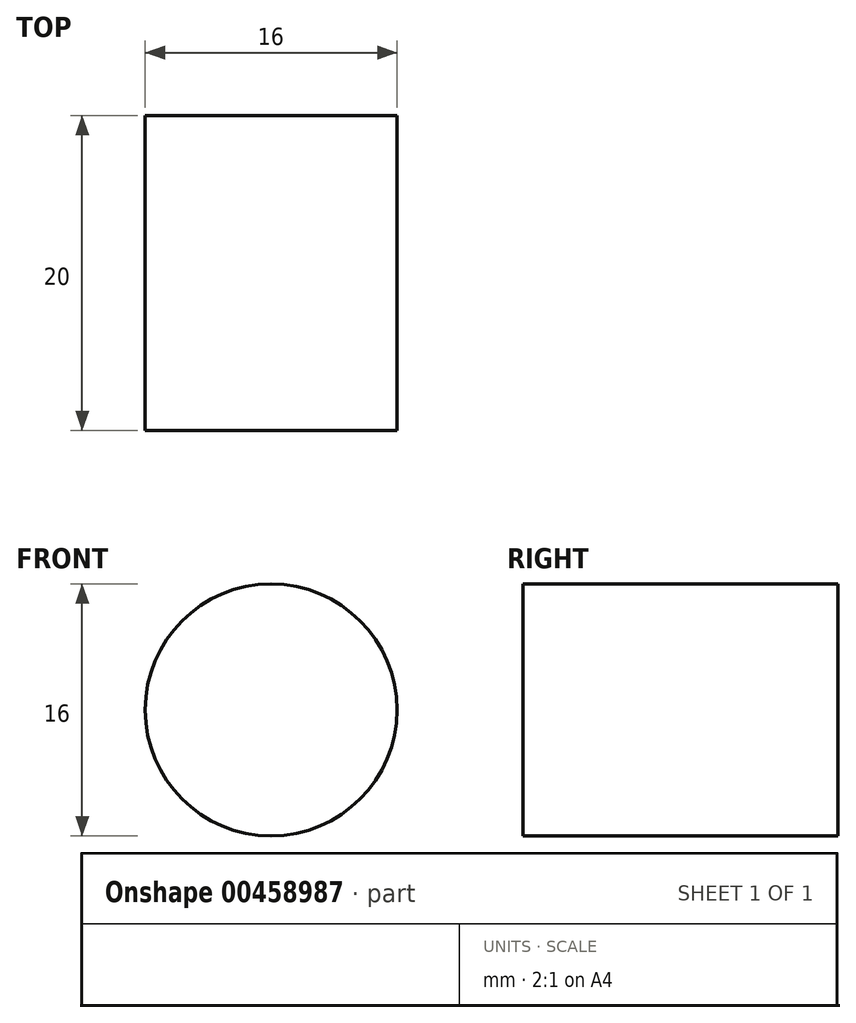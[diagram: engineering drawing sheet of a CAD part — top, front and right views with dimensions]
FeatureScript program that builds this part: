
annotation { "Feature Type Name" : "Feature", "Feature Type Description" : "" }
export const myFeature = defineFeature(function(context is Context, id is Id, definition is map)
    precondition{}
    {
        {
            var Q0;
            Q0=qCreatedBy(makeId("Front.planeOp"),FACE);
            var sketch = newSketch(context, id + "F0", { "sketchPlane" : qUnion([Q0])});
            skCircle(sketch, "E0", {"center": v(0, 0) * mm, "radius": 8 * mm});
            skSolve(sketch);
        }
        {
            var Q0;
            Q0 = qSketchRegion(id + "F0", true);
            extrude(context, id + "F1", {"entities" : qUnion([Q0]), "depth" : 20 * mm});
        }
    });
